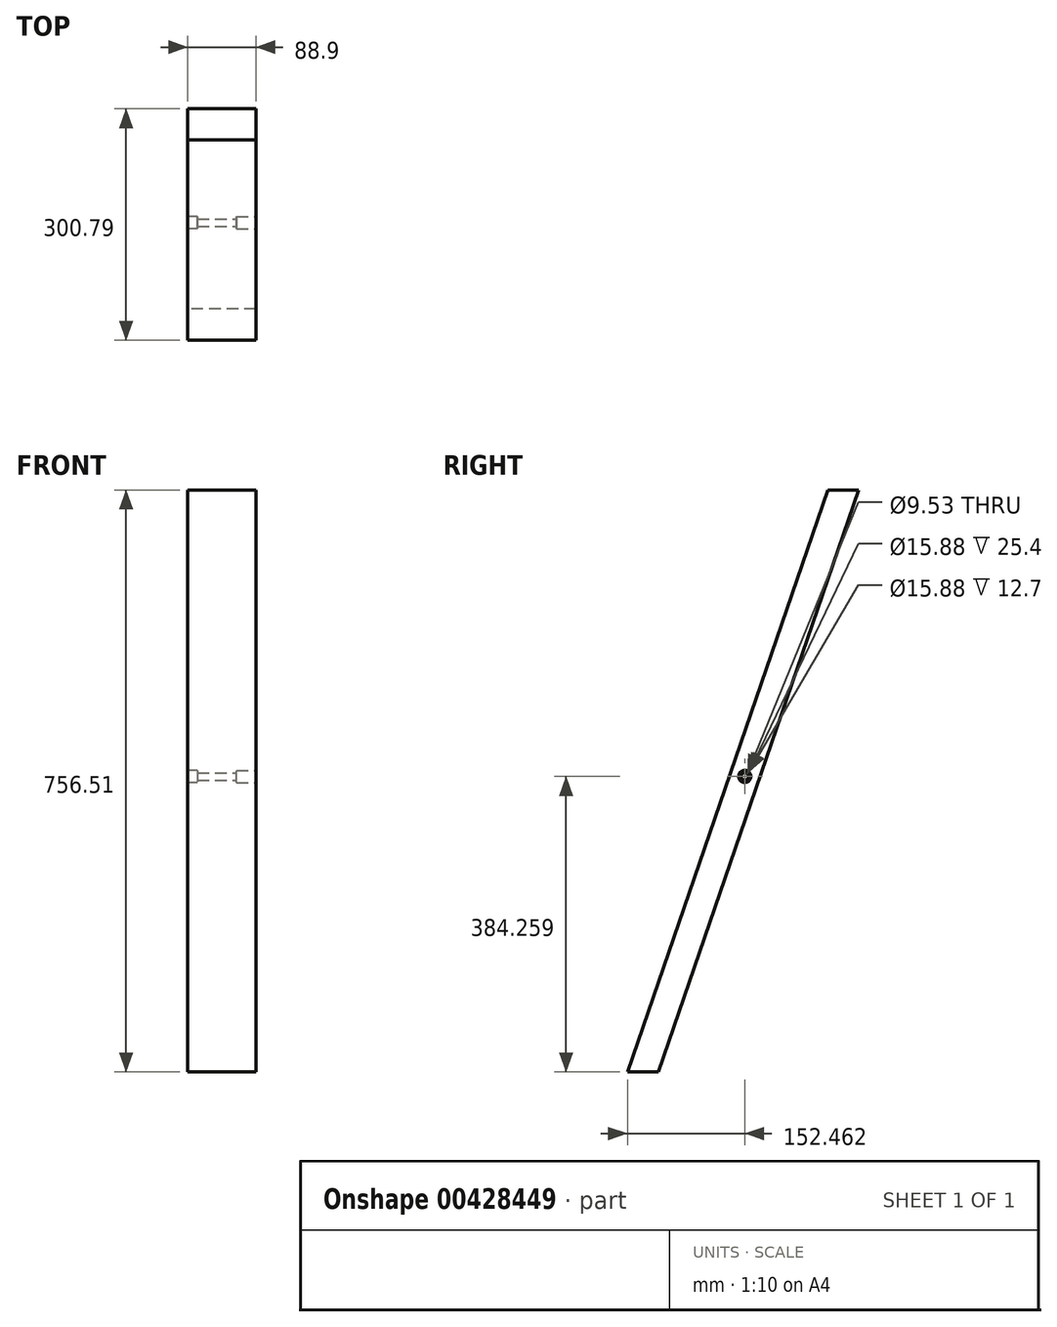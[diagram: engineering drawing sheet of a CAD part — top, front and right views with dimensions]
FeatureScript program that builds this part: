
annotation { "Feature Type Name" : "Feature", "Feature Type Description" : "" }
export const myFeature = defineFeature(function(context is Context, id is Id, definition is map)
    precondition{}
    {
        {
            var Q0;
            Q0=qCreatedBy(makeId("Right.planeOp"),FACE);
            var sketch = newSketch(context, id + "F0", { "sketchPlane" : qUnion([Q0])});
            skLineSegment(sketch, "E0", {"start": v(-4.15, -19.05) * mm, "end": v(-44.45, -19.05) * mm});
            skLineSegment(sketch, "E1", {"start": v(-44.45, -19.05) * mm, "end": v(-304.94, -775.56) * mm});
            skLineSegment(sketch, "E2", {"start": v(-304.94, -775.56) * mm, "end": v(-264.64, -775.56) * mm});
            skLineSegment(sketch, "E3", {"start": v(-4.15, -19.05) * mm, "end": v(-264.64, -775.56) * mm});
            skLineSegment(sketch, "E4", {"start": v(-289.82, -731.66) * mm, "end": v(-253.8, -744.07) * mm});
            skSolve(sketch);
        }
        {
            var Q0;
            Q0 = qSketchRegion(id + "F0", true);
            extrude(context, id + "F1", {"entities" : qUnion([Q0]), "depth" : 44.45 * mm, "hasSecondDirection" : true, "secondDirectionOppositeDirection" : true, "secondDirectionDepth" : 44.45 * mm});
        }
        {
            var Q0;
            Q0=makeQuery(id+"F1.opExtrude","CAP_FACE",FACE,{"disambiguationData":[OSD([sQuery(id+"F0.wireOp",EDGE,"E0"),sQuery(id+"F0.wireOp",EDGE,"E1"),sQuery(id+"F0.wireOp",EDGE,"E2"),sQuery(id+"F0.wireOp",EDGE,"E3")])],"isStart":false});
            var sketch = newSketch(context, id + "F2", { "sketchPlane" : qUnion([Q0])});
            skPoint(sketch, "E5", {"position": v(-152.48, -391.3) * mm});
            skSolve(sketch);
        }
        {
            var Q0;
            Q0=sQuery(id+"F2.wireOp",VERTEX,"E5");
            var Q1;
            Q1=makeQuery(id+"F1.opExtrude","SWEPT_BODY",BODY,{"disambiguationData":[OSD([sQuery(id+"F0.wireOp",EDGE,"E0"),sQuery(id+"F0.wireOp",EDGE,"E1"),sQuery(id+"F0.wireOp",EDGE,"E2"),sQuery(id+"F0.wireOp",EDGE,"E3")])]});
            hole(context, id + "F3", {"style" : HoleStyle.C_BORE, "endStyle" : HoleEndStyle.BLIND, "holeDiameter" : 9.52 * mm, "cBoreDiameter" : 15.88 * mm, "cBoreDepth" : 25.4 * mm, "holeDepth" : 31.75 * mm, "isTappedThrough" : true, "tappedDepth" : 12.7 * mm, "tapClearance" : 3, "locations" : qUnion([Q0]), "scope" : qUnion([Q1])});
        }
        {
            var Q0;
            Q0=makeQuery(id+"F1.opExtrude","CAP_FACE",FACE,{"disambiguationData":[OSD([sQuery(id+"F0.wireOp",EDGE,"E0"),sQuery(id+"F0.wireOp",EDGE,"E1"),sQuery(id+"F0.wireOp",EDGE,"E2"),sQuery(id+"F0.wireOp",EDGE,"E3")])],"isStart":true});
            var sketch = newSketch(context, id + "F4", { "sketchPlane" : qUnion([Q0])});
            skPoint(sketch, "E6", {"position": v(152.48, -391.3) * mm});
            skSolve(sketch);
        }
        {
            var Q0;
            Q0=sQuery(id+"F4.wireOp",VERTEX,"E6");
            var Q1;
            Q1=makeQuery(id+"F1.opExtrude","SWEPT_BODY",BODY,{"disambiguationData":[OSD([sQuery(id+"F0.wireOp",EDGE,"E0"),sQuery(id+"F0.wireOp",EDGE,"E1"),sQuery(id+"F0.wireOp",EDGE,"E2"),sQuery(id+"F0.wireOp",EDGE,"E3")])]});
            hole(context, id + "F5", {"style" : HoleStyle.C_BORE, "endStyle" : HoleEndStyle.THROUGH, "holeDiameter" : 9.52 * mm, "cBoreDiameter" : 15.88 * mm, "cBoreDepth" : 12.7 * mm, "isTappedThrough" : true, "tappedDepth" : 12.7 * mm, "tapClearance" : 3, "locations" : qUnion([Q0]), "scope" : qUnion([Q1])});
        }
    });
